# Revit family: P300150-031-30
name_source: partatom
category: Lighting Fixtures
revit_build: Autodesk Revit 2014 (Build: 20130308_1515(x64)
units: mm (PartAtom-declared; Revit-internal decimal feet)

## types (1)
- P300150-031-30
    Apparent Load = 36 VA
    Assembly Code = D5020200
    Color Filter = 16777215
    Connector Description = Lighting Connector
    Default Elevation = 48"
    Depth = 1 3/4"
    Description = Enjoy this bath fixture's classic forms with crisp, contemporary updates. A classic black finish coats a simple backplate that anchors the light fixture in place. An elegant etched white glass shade shaped in a thin cylinder stretches horizontally across the design for a clean, modern demeanor.
    Dimming Lamp Color Temperature Shift = <None>
    Fixture distribution = Direct
    Glass = Hubbell - Glass
    Height = 4 3/4"
    Housing Material = Paint - Hubbell - Textured Camera Black
    Lamp = LED
    Load Classification = Lighting
    Manufacturer = Progress Lighting
    Model = P300150-031-30
    Photometric Web File = generic
    Power Factor = 1
    Product Documentation Link = https://hubbellcdn.com
    Product Link = https://www.hubbell.com
    Specifications = An elegant etched white glass shade shaped in a thin cylinder stretches horizontally across the design.
A classic black finish coats a simple backplate that anchors the light fixture in place.
Enjoy classic forms with crisp, contemporary updates.
Ideal for any bathroom.
Perfect for mid-century modern, transitional, modern, and contemporary settings.
Measures 22-1/4-inch width by 4-3/4-inch height.
Uses an integrated LED (36w).
Compatible with many Triac/ELV dimmers (see dimming controls)
Includes installation instructions and mounting hardware.
Progress Lighting products are designed for exceptional quality, reliability, and functionality.
    Tilt Angle = 60.00°
    URL = https://www.hubbell.com
    Voltage = 120 V
    Warranty = 5 years Warranty
    Wattage Comments = 36
    Watts = 36 W
    Width = 22 1/4"

## geometry (parser evidence)
native form markers: Sweep x3
no freeform markers — native parametric forms only
